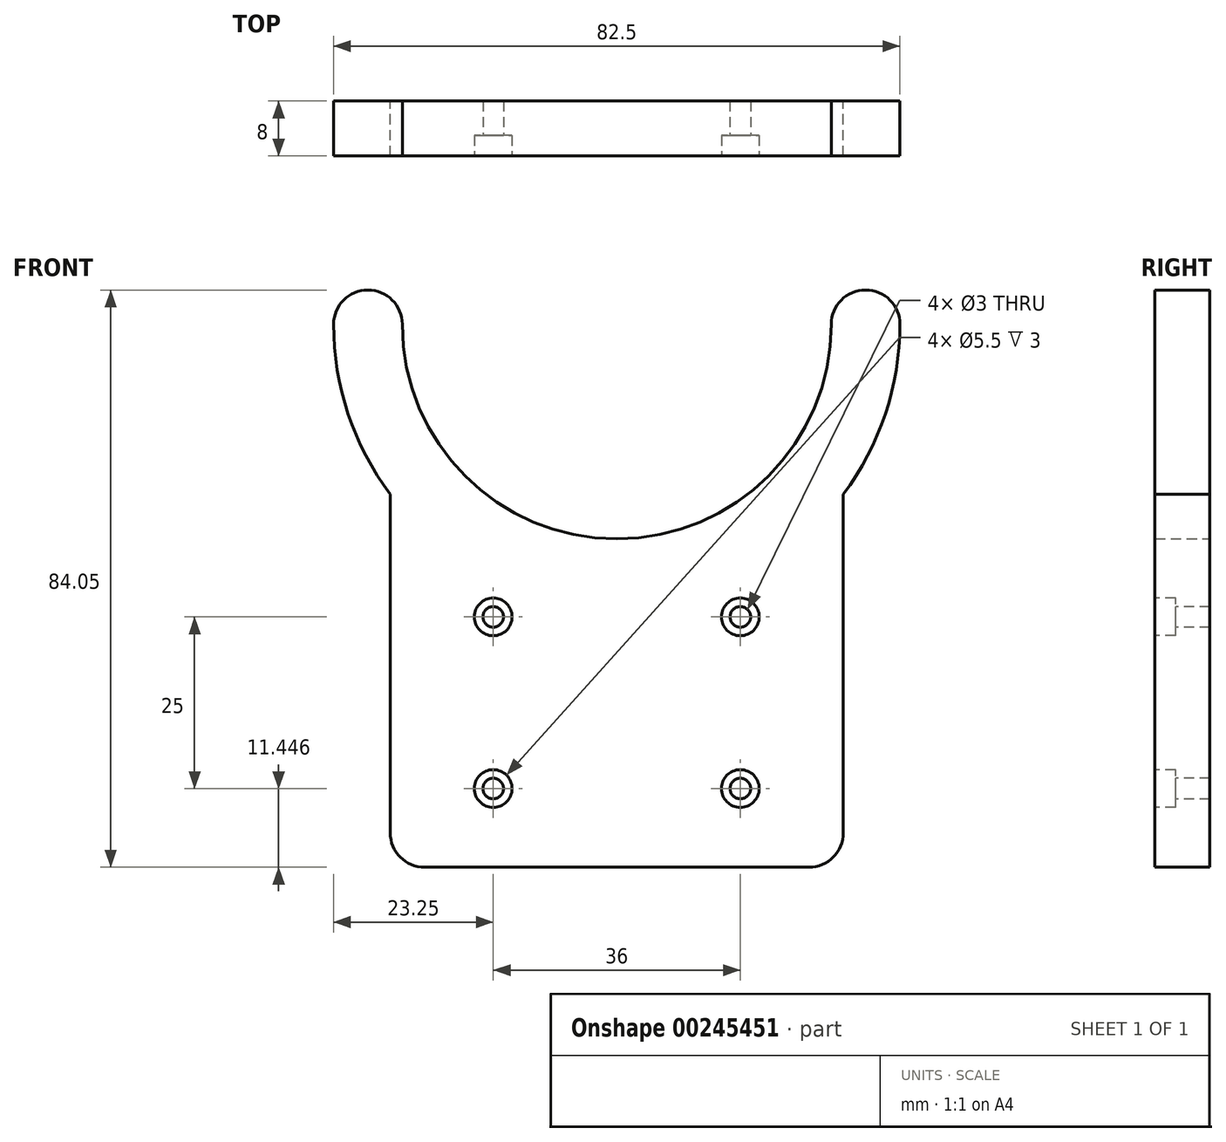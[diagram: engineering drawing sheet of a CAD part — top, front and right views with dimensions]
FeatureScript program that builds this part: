
annotation { "Feature Type Name" : "Feature", "Feature Type Description" : "" }
export const myFeature = defineFeature(function(context is Context, id is Id, definition is map)
    precondition{}
    {
        {
            var Q0;
            Q0=qCreatedBy(makeId("Front.planeOp"),FACE);
            var sketch = newSketch(context, id + "F0", { "sketchPlane" : qUnion([Q0])});
            skLineSegment(sketch, "E0.top", {"start": v(-33, -79.05) * mm, "end": v(33, -79.05) * mm});
            skLineSegment(sketch, "E0.left", {"start": v(-33, -24.75) * mm, "end": v(-33, -79.05) * mm});
            skLineSegment(sketch, "E0.right", {"start": v(33, -24.75) * mm, "end": v(33, -79.05) * mm});
            skArc(sketch, "E1", {"start": v(-31.25, 0) * mm, "mid": v(0, -31.25) * mm, "end": v(31.25, 0) * mm});
            skArc(sketch, "E2", {"start": v(33, -24.75) * mm, "mid": v(39.13, -13.04) * mm, "end": v(41.25, 0) * mm});
            skLineSegment(sketch, "E3", {"start": v(0, 0) * mm, "end": v(0, 7.66) * mm});
            skArc(sketch, "E4", {"start": v(-31.25, 0) * mm, "mid": v(-36.25, 5) * mm, "end": v(-41.25, 0) * mm});
            skArc(sketch, "E5.MirrorCS", {"start": v(31.25, 0) * mm, "mid": v(36.25, 5) * mm, "end": v(41.25, 0) * mm});
            skArc(sketch, "E6.trimOffspring", {"start": v(-41.25, 0) * mm, "mid": v(-39.13, -13.04) * mm, "end": v(-33, -24.75) * mm});
            skSolve(sketch);
        }
        {
            var Q0;
            Q0=qSketchRegion(id+"F0",true);
            extrude(context, id + "F1", {"entities" : qUnion([Q0]), "depth" : 8 * mm});
        }
        {
            var Q0;
            Q0=makeQuery(id+"F1.opExtrude","CAP_FACE",FACE,{"disambiguationData":[OSD([sQuery(id+"F0.wireOp",EDGE,"fee31f99-f0a1-4a59-91b9-d88257928f22.0"),sQuery(id+"F0.wireOp",EDGE,"fee31f99-f0a1-4a59-91b9-d88257928f22.1"),sQuery(id+"F0.wireOp",EDGE,"fee31f99-f0a1-4a59-91b9-d88257928f22.2"),sQuery(id+"F0.wireOp",EDGE,"fee31f99-f0a1-4a59-91b9-d88257928f22.3"),sQuery(id+"F0.wireOp",EDGE,"fee31f99-f0a1-4a59-91b9-d88257928f22.4"),sQuery(id+"F0.wireOp",EDGE,"fee31f99-f0a1-4a59-91b9-d88257928f22.5"),sQuery(id+"F0.wireOp",EDGE,"8316afb8-1114-43b2-b528-e6bb7452338e.0"),sQuery(id+"F0.wireOp",EDGE,"8316afb8-1114-43b2-b528-e6bb7452338e.3"),sQuery(id+"F0.wireOp",EDGE,"8316afb8-1114-43b2-b528-e6bb7452338e.4"),sQuery(id+"F0.wireOp",EDGE,"8316afb8-1114-43b2-b528-e6bb7452338e.5"),sQuery(id+"F0.wireOp",EDGE,"E0.top"),sQuery(id+"F0.wireOp",EDGE,"E0.left"),sQuery(id+"F0.wireOp",EDGE,"E0.right")])],"isStart":false});
            var sketch = newSketch(context, id + "F2", { "sketchPlane" : qUnion([Q0])});
            skCircle(sketch, "E7", {"center": v(18, -42.6) * mm, "radius": 1.5 * mm});
            skCircle(sketch, "E8", {"center": v(-18, -42.6) * mm, "radius": 1.5 * mm});
            skCircle(sketch, "E9", {"center": v(-18, -67.6) * mm, "radius": 1.5 * mm});
            skCircle(sketch, "E10", {"center": v(18, -67.6) * mm, "radius": 1.5 * mm});
            skSolve(sketch);
        }
        {
            var Q0;
            Q0=qSketchRegion(id+"F2",true);
            extrude(context, id + "F3", {"entities" : qUnion([Q0]), "operationType" : NewBodyOperationType.REMOVE, "oppositeDirection" : true, "depth" : 25 * mm});
        }
        {
            var Q0;
            Q0=makeQuery(id+"F1.opExtrude","CAP_FACE",FACE,{"disambiguationData":[OSD([sQuery(id+"F0.wireOp",EDGE,"fee31f99-f0a1-4a59-91b9-d88257928f22.0"),sQuery(id+"F0.wireOp",EDGE,"fee31f99-f0a1-4a59-91b9-d88257928f22.1"),sQuery(id+"F0.wireOp",EDGE,"fee31f99-f0a1-4a59-91b9-d88257928f22.2"),sQuery(id+"F0.wireOp",EDGE,"fee31f99-f0a1-4a59-91b9-d88257928f22.3"),sQuery(id+"F0.wireOp",EDGE,"fee31f99-f0a1-4a59-91b9-d88257928f22.4"),sQuery(id+"F0.wireOp",EDGE,"fee31f99-f0a1-4a59-91b9-d88257928f22.5"),sQuery(id+"F0.wireOp",EDGE,"8316afb8-1114-43b2-b528-e6bb7452338e.0"),sQuery(id+"F0.wireOp",EDGE,"8316afb8-1114-43b2-b528-e6bb7452338e.3"),sQuery(id+"F0.wireOp",EDGE,"8316afb8-1114-43b2-b528-e6bb7452338e.4"),sQuery(id+"F0.wireOp",EDGE,"8316afb8-1114-43b2-b528-e6bb7452338e.5"),sQuery(id+"F0.wireOp",EDGE,"E0.top"),sQuery(id+"F0.wireOp",EDGE,"E0.left"),sQuery(id+"F0.wireOp",EDGE,"E0.right")])],"isStart":false});
            var sketch = newSketch(context, id + "F4", { "sketchPlane" : qUnion([Q0])});
            skCircle(sketch, "E11", {"center": v(-18, -42.6) * mm, "radius": 2.75 * mm});
            skCircle(sketch, "E12", {"center": v(18, -42.6) * mm, "radius": 2.75 * mm});
            skCircle(sketch, "E13", {"center": v(18, -67.6) * mm, "radius": 2.75 * mm});
            skCircle(sketch, "E14", {"center": v(-18, -67.6) * mm, "radius": 2.75 * mm});
            skSolve(sketch);
        }
        {
            var Q0;
            Q0=qSketchRegion(id+"F4",true);
            extrude(context, id + "F5", {"entities" : qUnion([Q0]), "operationType" : NewBodyOperationType.REMOVE, "oppositeDirection" : true, "depth" : 3 * mm});
        }
        {
            var Q0;
            Q0=makeQuery(id+"F1.opExtrude","SWEPT_EDGE",EDGE,{"disambiguationData":[OSD([sQuery(id+"F0.wireOp",EDGE,"E0.top"),sQuery(id+"F0.wireOp",EDGE,"E0.right")])]});
            var Q1;
            Q1=makeQuery(id+"F1.opExtrude","SWEPT_EDGE",EDGE,{"disambiguationData":[OSD([sQuery(id+"F0.wireOp",EDGE,"E0.top"),sQuery(id+"F0.wireOp",EDGE,"E0.left")])]});
            fillet(context, id + "F6", {"entities" : qUnion([Q0, Q1]), "radius" : 5 * mm, "tangentPropagation" : true, "allowEdgeOverflow" : false});
        }
    });
